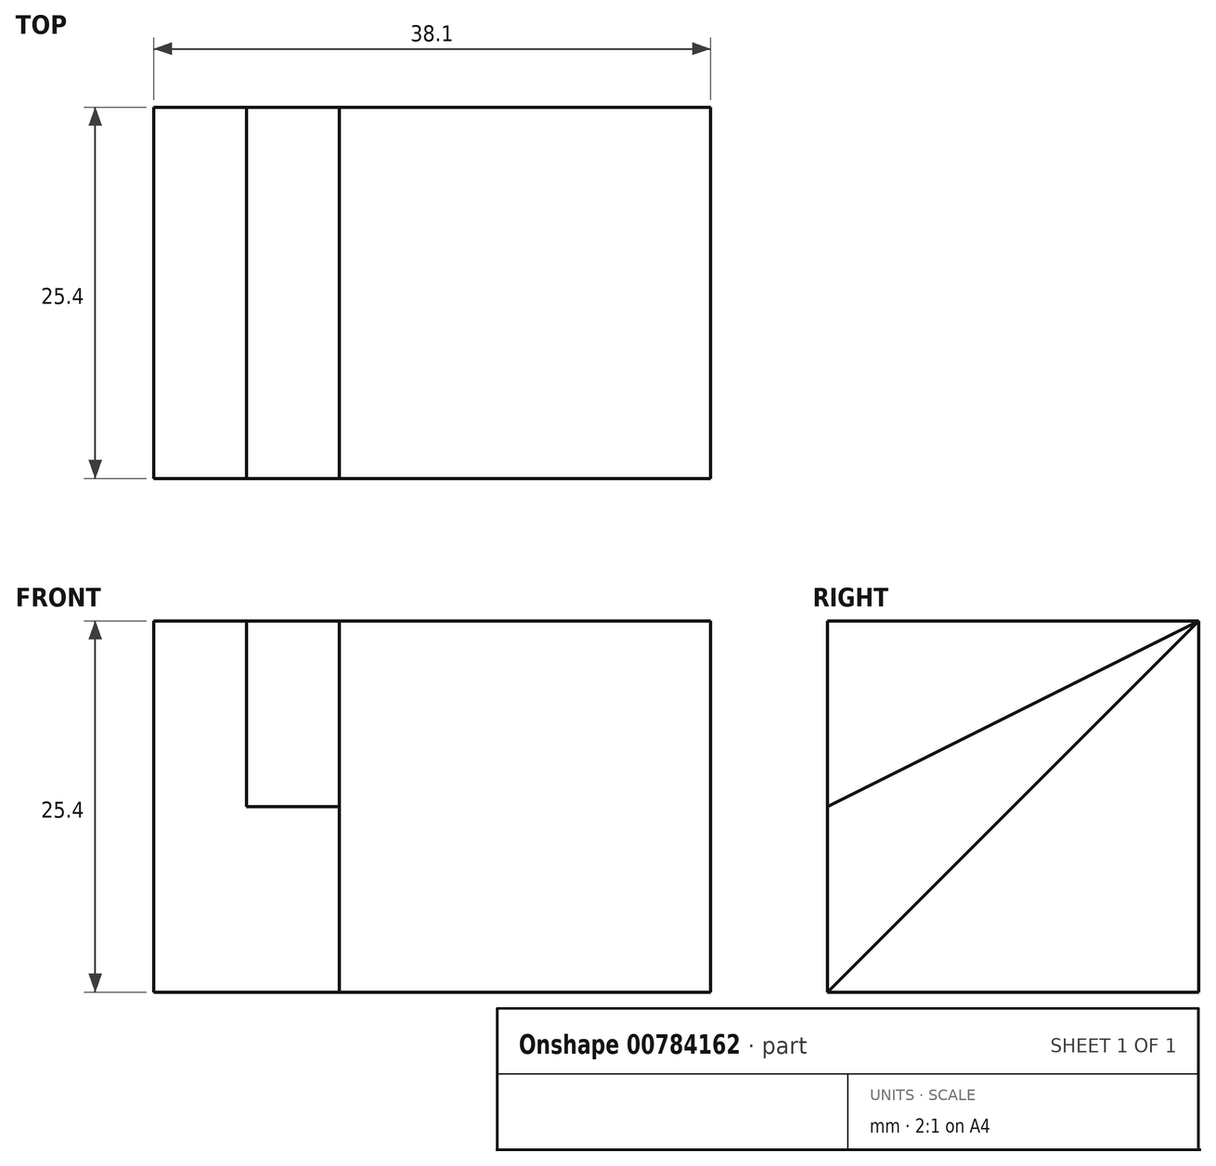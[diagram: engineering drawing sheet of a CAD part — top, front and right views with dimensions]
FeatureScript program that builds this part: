
annotation { "Feature Type Name" : "Feature", "Feature Type Description" : "" }
export const myFeature = defineFeature(function(context is Context, id is Id, definition is map)
    precondition{}
    {
        {
            var Q0;
            Q0=qCreatedBy(makeId("Front.planeOp"),FACE);
            var sketch = newSketch(context, id + "F0", { "sketchPlane" : qUnion([Q0])});
            skLineSegment(sketch, "E0", {"start": v(0, 0) * mm, "end": v(38.1, 0) * mm});
            skLineSegment(sketch, "E1", {"start": v(0, 0) * mm, "end": v(0, 25.4) * mm});
            skLineSegment(sketch, "E2", {"start": v(0, 25.4) * mm, "end": v(38.1, 25.4) * mm});
            skLineSegment(sketch, "E3", {"start": v(38.1, 25.4) * mm, "end": v(38.1, 0) * mm});
            skSolve(sketch);
        }
        {
            var Q0;
            Q0=makeQuery(id+"F0.imprint","IMPRINT",FACE,{"disambiguationData":[TD([[makeQuery(id+"F0.imprint","IMPRINT",EDGE,{"derivedFrom":sQuery(id+"F0.wireOp",EDGE,"E0")}),1.0]])]});
            extrude(context, id + "F1", {"entities" : qUnion([Q0]), "depth" : 25.4 * mm, "offsetDistance" : 25.4 * mm});
        }
        {
            var Q0;
            Q0=makeQuery(id+"F1.opExtrude","SWEPT_FACE",FACE,{"disambiguationData":[OSD([sQuery(id+"F0.wireOp",EDGE,"E3")])]});
            var sketch = newSketch(context, id + "F2", { "sketchPlane" : qUnion([Q0])});
            skLineSegment(sketch, "E4", {"start": v(0, 25.4) * mm, "end": v(-25.4, 0) * mm});
            skSolve(sketch);
        }
        {
            var Q0;
            Q0 = qSketchRegion(id + "F2", true);
            var Q1;
            Q1=makeQuery(id+"F2.imprint","IMPRINT",FACE,{"disambiguationData":[TD([[makeQuery(id+"F2.imprint","IMPRINT",EDGE,{"derivedFrom":sQuery(id+"F2.wireOp",EDGE,"E4")}),-1.0]])]});
            extrude(context, id + "F3", {"entities" : qUnion([Q0, Q1]), "operationType" : NewBodyOperationType.REMOVE, "oppositeDirection" : true, "depth" : 25.4 * mm, "offsetDistance" : 25.4 * mm});
        }
        {
            var Q0;
            Q0=makeQuery(id+"F3.boolean.opBoolean","COPY",FACE,{"derivedFrom":makeQuery(id+"F3.opExtrude","CAP_FACE",FACE,{"disambiguationData":[OSD([sQuery(id+"F0.wireOp",EDGE,"E2"),sQuery(id+"F0.wireOp",EDGE,"E3"),sQuery(id+"F2.wireOp",EDGE,"E4")])],"isStart":false})});
            var sketch = newSketch(context, id + "F4", { "sketchPlane" : qUnion([Q0])});
            skLineSegment(sketch, "E5", {"start": v(-25.4, 25.4) * mm, "end": v(-25.4, 12.7) * mm});
            skLineSegment(sketch, "E6", {"start": v(-25.4, 12.7) * mm, "end": v(0, 25.4) * mm});
            skLineSegment(sketch, "E7", {"start": v(0, 25.4) * mm, "end": v(-25.4, 25.4) * mm});
            skSolve(sketch);
        }
        {
            var Q0;
            Q0=makeQuery(id+"F4.imprint","IMPRINT",FACE,{"disambiguationData":[TD([[makeQuery(id+"F4.imprint","IMPRINT",EDGE,{"derivedFrom":sQuery(id+"F4.wireOp",EDGE,"E5")}),1.0]])]});
            extrude(context, id + "F5", {"entities" : qUnion([Q0]), "operationType" : NewBodyOperationType.REMOVE, "oppositeDirection" : true, "depth" : 6.35 * mm, "offsetDistance" : 25.4 * mm});
        }
    });
